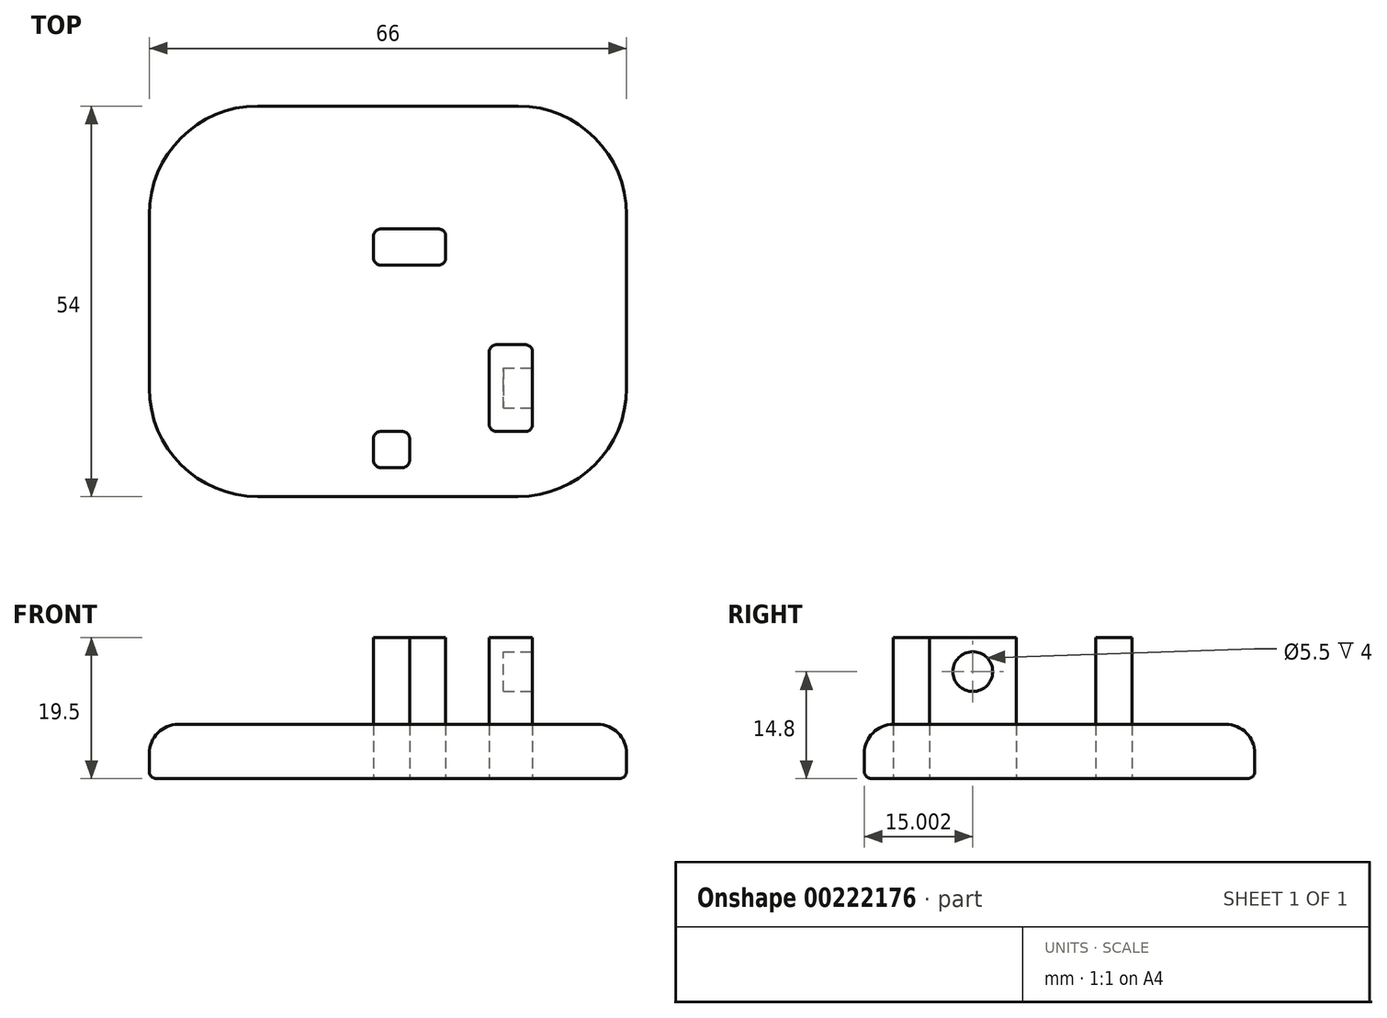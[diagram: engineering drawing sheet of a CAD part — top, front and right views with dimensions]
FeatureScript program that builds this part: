
annotation { "Feature Type Name" : "Feature", "Feature Type Description" : "" }
export const myFeature = defineFeature(function(context is Context, id is Id, definition is map)
    precondition{}
    {
        {
            var Q0;
            Q0=qCreatedBy(makeId("Top.planeOp"),FACE);
            var sketch = newSketch(context, id + "F0", { "sketchPlane" : qUnion([Q0])});
            skLineSegment(sketch, "E0.bottom", {"start": v(-30.44, 33.23) * mm, "end": v(35.56, 33.23) * mm});
            skLineSegment(sketch, "E0.top", {"start": v(-30.44, -20.77) * mm, "end": v(35.56, -20.77) * mm});
            skLineSegment(sketch, "E0.left", {"start": v(-30.44, 33.23) * mm, "end": v(-30.44, -20.77) * mm});
            skLineSegment(sketch, "E0.right", {"start": v(35.56, 33.23) * mm, "end": v(35.56, -20.77) * mm});
            skSolve(sketch);
        }
        {
            var Q0;
            Q0=makeQuery(id+"F0.imprint","IMPRINT",FACE,{"disambiguationData":[TD([[makeQuery(id+"F0.imprint","IMPRINT",EDGE,{"derivedFrom":sQuery(id+"F0.wireOp",EDGE,"E0.bottom")}),-1.0]])]});
            extrude(context, id + "F1", {"entities" : qUnion([Q0]), "depth" : 7.5 * mm});
        }
        {
            var Q0;
            Q0=makeQuery(id+"F1.opExtrude","CAP_FACE",FACE,{"disambiguationData":[OSD([sQuery(id+"F0.wireOp",EDGE,"E0.bottom"),sQuery(id+"F0.wireOp",EDGE,"E0.top"),sQuery(id+"F0.wireOp",EDGE,"E0.left"),sQuery(id+"F0.wireOp",EDGE,"E0.right")])],"isStart":false});
            fillet(context, id + "F2", {"entities" : qUnion([Q0]), "radius" : 4 * mm, "tangentPropagation" : true, "allowEdgeOverflow" : false});
        }
        {
            var Q0;
            Q0=makeQuery(id+"F1.opExtrude","CAP_FACE",FACE,{"disambiguationData":[OSD([sQuery(id+"F0.wireOp",EDGE,"E0.bottom"),sQuery(id+"F0.wireOp",EDGE,"E0.top"),sQuery(id+"F0.wireOp",EDGE,"E0.left"),sQuery(id+"F0.wireOp",EDGE,"E0.right")])],"isStart":true});
            fillet(context, id + "F3", {"entities" : qUnion([Q0]), "radius" : 1 * mm, "tangentPropagation" : true, "allowEdgeOverflow" : false});
        }
        {
            var Q0;
            Q0=qCreatedBy(makeId("Top.planeOp"),FACE);
            var sketch = newSketch(context, id + "F4", { "sketchPlane" : qUnion([Q0])});
            skLineSegment(sketch, "E1.bottom", {"start": v(16.56, 0.23) * mm, "end": v(22.56, 0.23) * mm});
            skLineSegment(sketch, "E1.top", {"start": v(16.56, -11.77) * mm, "end": v(22.56, -11.77) * mm});
            skLineSegment(sketch, "E1.left", {"start": v(16.56, 0.23) * mm, "end": v(16.56, -11.77) * mm});
            skLineSegment(sketch, "E1.right", {"start": v(22.56, 0.23) * mm, "end": v(22.56, -11.77) * mm});
            skLineSegment(sketch, "E2.bottom", {"start": v(0.56, 16.23) * mm, "end": v(10.56, 16.23) * mm});
            skLineSegment(sketch, "E2.top", {"start": v(0.56, 11.23) * mm, "end": v(10.56, 11.23) * mm});
            skLineSegment(sketch, "E2.left", {"start": v(0.56, 16.23) * mm, "end": v(0.56, 11.23) * mm});
            skLineSegment(sketch, "E2.right", {"start": v(10.56, 16.23) * mm, "end": v(10.56, 11.23) * mm});
            skLineSegment(sketch, "E3.bottom", {"start": v(0.56, -11.77) * mm, "end": v(5.56, -11.77) * mm});
            skLineSegment(sketch, "E3.top", {"start": v(0.56, -16.77) * mm, "end": v(5.56, -16.77) * mm});
            skLineSegment(sketch, "E3.left", {"start": v(0.56, -11.77) * mm, "end": v(0.56, -16.77) * mm});
            skLineSegment(sketch, "E3.right", {"start": v(5.56, -11.77) * mm, "end": v(5.56, -16.77) * mm});
            skLineSegment(sketch, "E4", {"start": v(-0.15, -11.77) * mm, "end": v(16.56, -11.77) * mm, "construction": true});
            skLineSegment(sketch, "E5", {"start": v(0.56, 31.2) * mm, "end": v(0.56, -45.77) * mm, "construction": true});
            skSolve(sketch);
        }
        {
            var Q0;
            Q0 = qSketchRegion(id + "F4", true);
            extrude(context, id + "F5", {"entities" : qUnion([Q0]), "depth" : 19.5 * mm});
        }
        {
            var Q0;
            Q0=makeQuery(id+"F5.opExtrude","SWEPT_EDGE",EDGE,{"disambiguationData":[OSD([sQuery(id+"F4.wireOp",EDGE,"E1.top"),sQuery(id+"F4.wireOp",EDGE,"E1.left")])]});
            var Q1;
            Q1=makeQuery(id+"F5.opExtrude","SWEPT_EDGE",EDGE,{"disambiguationData":[OSD([sQuery(id+"F4.wireOp",EDGE,"E1.top"),sQuery(id+"F4.wireOp",EDGE,"E1.right")])]});
            var Q2;
            Q2=makeQuery(id+"F5.opExtrude","SWEPT_EDGE",EDGE,{"disambiguationData":[OSD([sQuery(id+"F4.wireOp",EDGE,"E3.top"),sQuery(id+"F4.wireOp",EDGE,"E3.left")])]});
            var Q3;
            Q3=makeQuery(id+"F5.opExtrude","SWEPT_EDGE",EDGE,{"disambiguationData":[OSD([sQuery(id+"F4.wireOp",EDGE,"E3.top"),sQuery(id+"F4.wireOp",EDGE,"E3.right")])]});
            var Q4;
            Q4=makeQuery(id+"F5.opExtrude","SWEPT_EDGE",EDGE,{"disambiguationData":[OSD([sQuery(id+"F4.wireOp",EDGE,"E2.top"),sQuery(id+"F4.wireOp",EDGE,"E2.right")])]});
            var Q5;
            Q5=makeQuery(id+"F5.opExtrude","SWEPT_EDGE",EDGE,{"disambiguationData":[OSD([sQuery(id+"F4.wireOp",EDGE,"E2.top"),sQuery(id+"F4.wireOp",EDGE,"E2.left")])]});
            var Q6;
            Q6=makeQuery(id+"F5.opExtrude","SWEPT_EDGE",EDGE,{"disambiguationData":[OSD([sQuery(id+"F4.wireOp",EDGE,"E3.bottom"),sQuery(id+"F4.wireOp",EDGE,"E3.right")])]});
            var Q7;
            Q7=makeQuery(id+"F5.opExtrude","SWEPT_EDGE",EDGE,{"disambiguationData":[OSD([sQuery(id+"F4.wireOp",EDGE,"E1.bottom"),sQuery(id+"F4.wireOp",EDGE,"E1.right")])]});
            var Q8;
            Q8=makeQuery(id+"F5.opExtrude","SWEPT_EDGE",EDGE,{"disambiguationData":[OSD([sQuery(id+"F4.wireOp",EDGE,"E2.bottom"),sQuery(id+"F4.wireOp",EDGE,"E2.right")])]});
            var Q9;
            Q9=makeQuery(id+"F5.opExtrude","SWEPT_EDGE",EDGE,{"disambiguationData":[OSD([sQuery(id+"F4.wireOp",EDGE,"E2.bottom"),sQuery(id+"F4.wireOp",EDGE,"E2.left")])]});
            var Q10;
            Q10=makeQuery(id+"F5.opExtrude","SWEPT_EDGE",EDGE,{"disambiguationData":[OSD([sQuery(id+"F4.wireOp",EDGE,"E1.bottom"),sQuery(id+"F4.wireOp",EDGE,"E1.left")])]});
            var Q11;
            Q11=makeQuery(id+"F5.opExtrude","SWEPT_EDGE",EDGE,{"disambiguationData":[OSD([sQuery(id+"F4.wireOp",EDGE,"E3.bottom"),sQuery(id+"F4.wireOp",EDGE,"E3.left")])]});
            fillet(context, id + "F6", {"entities" : qUnion([Q0, Q1, Q2, Q3, Q4, Q5, Q6, Q7, Q8, Q9, Q10, Q11]), "radius" : 1 * mm, "tangentPropagation" : true, "allowEdgeOverflow" : false});
        }
        {
            var Q0;
            Q0=makeQuery(id+"F5.opExtrude","SWEPT_FACE",FACE,{"disambiguationData":[OSD([sQuery(id+"F4.wireOp",EDGE,"E1.right")])]});
            var sketch = newSketch(context, id + "F7", { "sketchPlane" : qUnion([Q0])});
            skCircle(sketch, "E6", {"center": v(-5.77, 14.8) * mm, "radius": 2.75 * mm});
            skLineSegment(sketch, "E7", {"start": v(-5.77, 19.5) * mm, "end": v(-5.77, -11.56) * mm, "construction": true});
            skPoint(sketch, "E7.endSnap0", {"position": v(-5.77, 0) * mm});
            skSolve(sketch);
        }
        {
            var Q0;
            Q0=makeQuery(id+"F7.imprint","IMPRINT",FACE,{"disambiguationData":[TD([[makeQuery(id+"F7.imprint","IMPRINT",EDGE,{"derivedFrom":sQuery(id+"F7.wireOp",EDGE,"E6")}),1.0]])]});
            extrude(context, id + "F8", {"entities" : qUnion([Q0]), "operationType" : NewBodyOperationType.REMOVE, "oppositeDirection" : true, "depth" : 4 * mm});
        }
        {
            var Q0;
            Q0=makeQuery(id+"F1.opExtrude","SWEPT_EDGE",EDGE,{"disambiguationData":[OSD([sQuery(id+"F0.wireOp",EDGE,"E0.top"),sQuery(id+"F0.wireOp",EDGE,"E0.right")])]});
            var Q1;
            Q1=makeQuery(id+"F1.opExtrude","SWEPT_EDGE",EDGE,{"disambiguationData":[OSD([sQuery(id+"F0.wireOp",EDGE,"E0.bottom"),sQuery(id+"F0.wireOp",EDGE,"E0.right")])]});
            var Q2;
            Q2=makeQuery(id+"F1.opExtrude","SWEPT_EDGE",EDGE,{"disambiguationData":[OSD([sQuery(id+"F0.wireOp",EDGE,"E0.bottom"),sQuery(id+"F0.wireOp",EDGE,"E0.left")])]});
            var Q3;
            Q3=makeQuery(id+"F1.opExtrude","SWEPT_EDGE",EDGE,{"disambiguationData":[OSD([sQuery(id+"F0.wireOp",EDGE,"E0.top"),sQuery(id+"F0.wireOp",EDGE,"E0.left")])]});
            fillet(context, id + "F9", {"entities" : qUnion([Q0, Q1, Q2, Q3]), "radius" : 15 * mm, "tangentPropagation" : true, "allowEdgeOverflow" : false});
        }
    });
